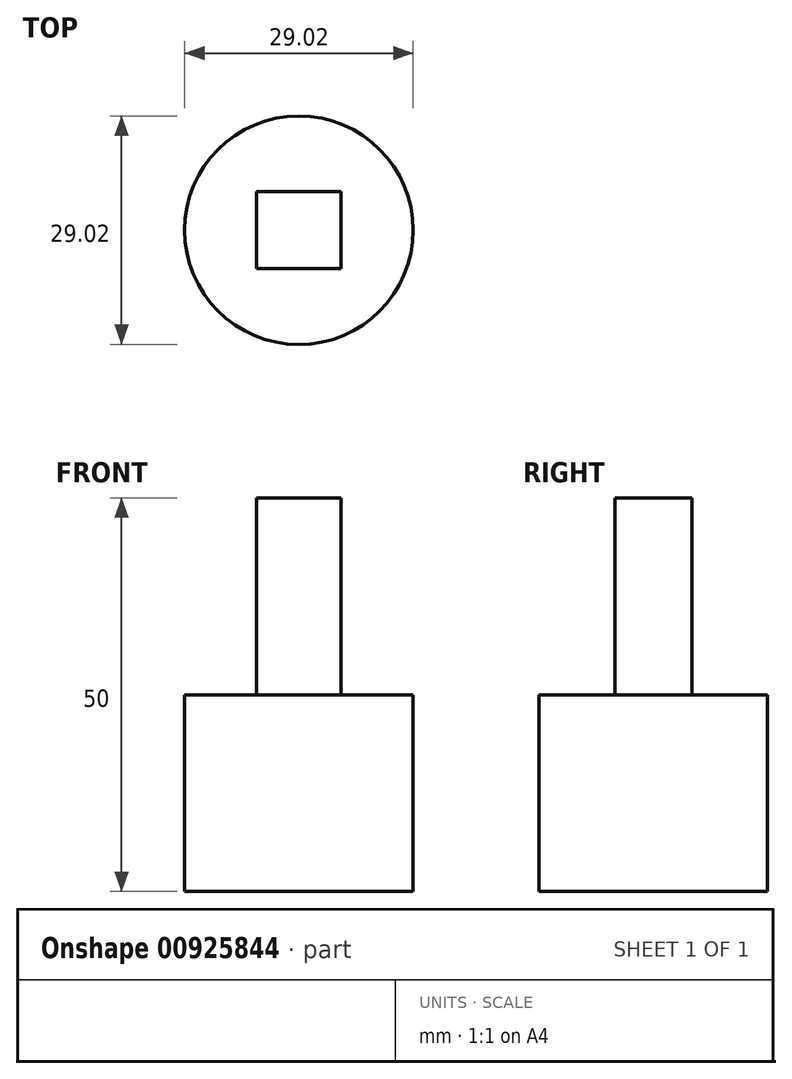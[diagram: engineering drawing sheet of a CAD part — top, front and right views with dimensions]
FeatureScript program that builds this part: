
annotation { "Feature Type Name" : "Feature", "Feature Type Description" : "" }
export const myFeature = defineFeature(function(context is Context, id is Id, definition is map)
    precondition{}
    {
        {
            var Q0;
            Q0=qCreatedBy(makeId("Top.planeOp"),FACE);
            var sketch = newSketch(context, id + "F0", { "sketchPlane" : qUnion([Q0])});
            skCircle(sketch, "E0", {"center": v(0, 0) * mm, "radius": 14.51 * mm});
            skSolve(sketch);
        }
        {
            var Q0;
            Q0 = qSketchRegion(id + "F0", true);
            extrude(context, id + "F1", {"entities" : qUnion([Q0]), "depth" : 25 * mm, "offsetDistance" : 25 * mm});
        }
        {
            var Q0;
            Q0=makeQuery(id+"F1.opExtrude","CAP_FACE",FACE,{"disambiguationData":[OSD([sQuery(id+"F0.wireOp",EDGE,"E0")])],"isStart":false});
            var sketch = newSketch(context, id + "F2", { "sketchPlane" : qUnion([Q0])});
            skLineSegment(sketch, "E1.bottom", {"start": v(5.38, -4.9) * mm, "end": v(-5.38, -4.9) * mm});
            skLineSegment(sketch, "E1.top", {"start": v(5.38, 4.9) * mm, "end": v(-5.38, 4.9) * mm});
            skLineSegment(sketch, "E1.left", {"start": v(5.38, -4.9) * mm, "end": v(5.38, 4.9) * mm});
            skLineSegment(sketch, "E1.right", {"start": v(-5.38, -4.9) * mm, "end": v(-5.38, 4.9) * mm});
            skPoint(sketch, "E1.middle", {"position": v(0, 0) * mm});
            skSolve(sketch);
        }
        {
            var Q0;
            Q0 = qSketchRegion(id + "F2", true);
            extrude(context, id + "F3", {"entities" : qUnion([Q0]), "depth" : 25 * mm, "offsetDistance" : 25 * mm});
        }
    });
